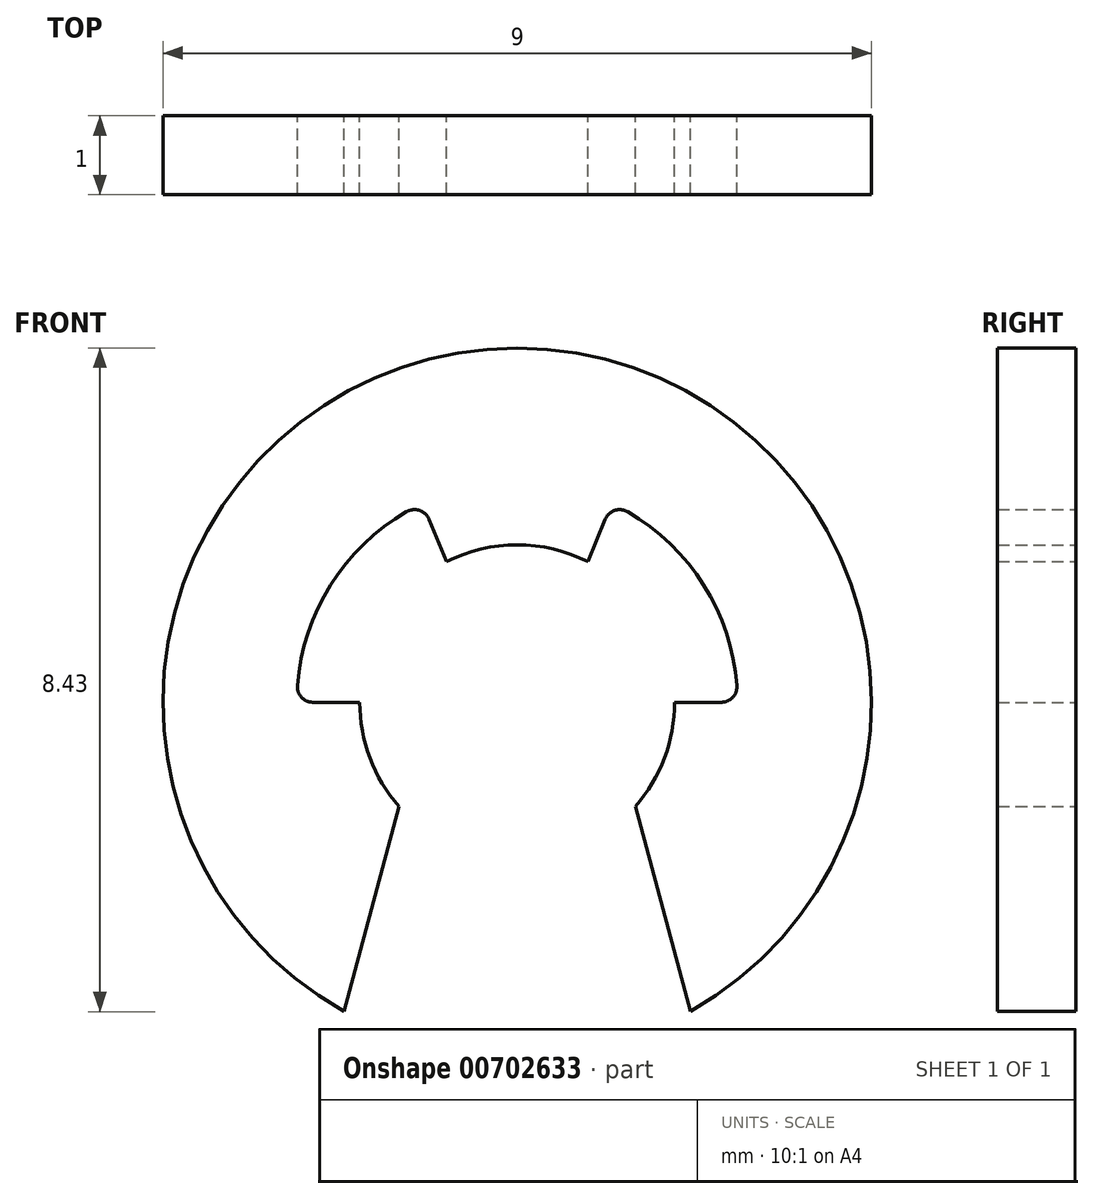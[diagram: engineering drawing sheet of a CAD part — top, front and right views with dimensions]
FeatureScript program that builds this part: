
annotation { "Feature Type Name" : "Feature", "Feature Type Description" : "" }
export const myFeature = defineFeature(function(context is Context, id is Id, definition is map)
    precondition{}
    {
        {
            var Q0;
            Q0=qCreatedBy(makeId("Front.planeOp"),FACE);
            var sketch = newSketch(context, id + "F0", { "sketchPlane" : qUnion([Q0])});
            skCircle(sketch, "E0", {"center": v(0, 0) * mm, "radius": 2 * mm});
            skCircle(sketch, "E1", {"center": v(0, 0) * mm, "radius": 4.5 * mm});
            skLineSegment(sketch, "E2", {"start": v(-1.5, -1.32) * mm, "end": v(-2.2, -3.93) * mm});
            skLineSegment(sketch, "E3", {"start": v(-2, 0) * mm, "end": v(-2.8, 0) * mm});
            skLineSegment(sketch, "E4", {"start": v(-0.9, 1.79) * mm, "end": v(-1.2, 2.53) * mm});
            skLineSegment(sketch, "E5", {"start": v(0, 0) * mm, "end": v(0, 4.25) * mm, "construction": true});
            skLineSegment(sketch, "E6", {"start": v(0, 0) * mm, "end": v(0, -4.4) * mm, "construction": true});
            skArc(sketch, "E7", {"start": v(-1.2, 2.53) * mm, "mid": v(-2.37, 1.5) * mm, "end": v(-2.8, 0) * mm});
            skLineSegment(sketch, "E8.MirrorCS", {"start": v(1.5, -1.32) * mm, "end": v(2.2, -3.93) * mm});
            skLineSegment(sketch, "E9.MirrorCS", {"start": v(0.9, 1.79) * mm, "end": v(1.2, 2.53) * mm});
            skLineSegment(sketch, "E10.MirrorCS", {"start": v(2, 0) * mm, "end": v(2.8, 0) * mm});
            skArc(sketch, "E11.MirrorCS", {"start": v(1.2, 2.53) * mm, "mid": v(2.37, 1.5) * mm, "end": v(2.8, 0) * mm});
            skSolve(sketch);
        }
        {
            var Q0;
            {var subQ3=sQuery(id+"F0.wireOp",EDGE,"E2");Q0=makeQuery(id+"F0.imprint","IMPRINT",FACE,{"disambiguationData":[TD([[makeQuery(id+"F0.imprint","IMPRINT",EDGE,{"derivedFrom":subQ3}),-1.0]])]});}
            extrude(context, id + "F1", {"entities" : qUnion([Q0]), "depth" : 1 * mm, "offsetDistance" : 25 * mm});
        }
        {
            var Q0;
            Q0=makeQuery(id+"F1.opExtrude","SWEPT_EDGE",EDGE,{"disambiguationData":[OSD([sQuery(id+"F0.wireOp",EDGE,"E4"),sQuery(id+"F0.wireOp",EDGE,"E7")])]});
            var Q1;
            Q1=makeQuery(id+"F1.opExtrude","SWEPT_EDGE",EDGE,{"disambiguationData":[OSD([sQuery(id+"F0.wireOp",EDGE,"E9.MirrorCS"),sQuery(id+"F0.wireOp",EDGE,"E11.MirrorCS")])]});
            var Q2;
            Q2=makeQuery(id+"F1.opExtrude","SWEPT_EDGE",EDGE,{"disambiguationData":[OSD([sQuery(id+"F0.wireOp",EDGE,"E10.MirrorCS"),sQuery(id+"F0.wireOp",EDGE,"E11.MirrorCS")])]});
            var Q3;
            Q3=makeQuery(id+"F1.opExtrude","SWEPT_EDGE",EDGE,{"disambiguationData":[OSD([sQuery(id+"F0.wireOp",EDGE,"E3"),sQuery(id+"F0.wireOp",EDGE,"E7")])]});
            fillet(context, id + "F2", {"entities" : qUnion([Q0, Q1, Q2, Q3]), "radius" : 0.2 * mm, "tangentPropagation" : true, "allowEdgeOverflow" : false});
        }
    });
